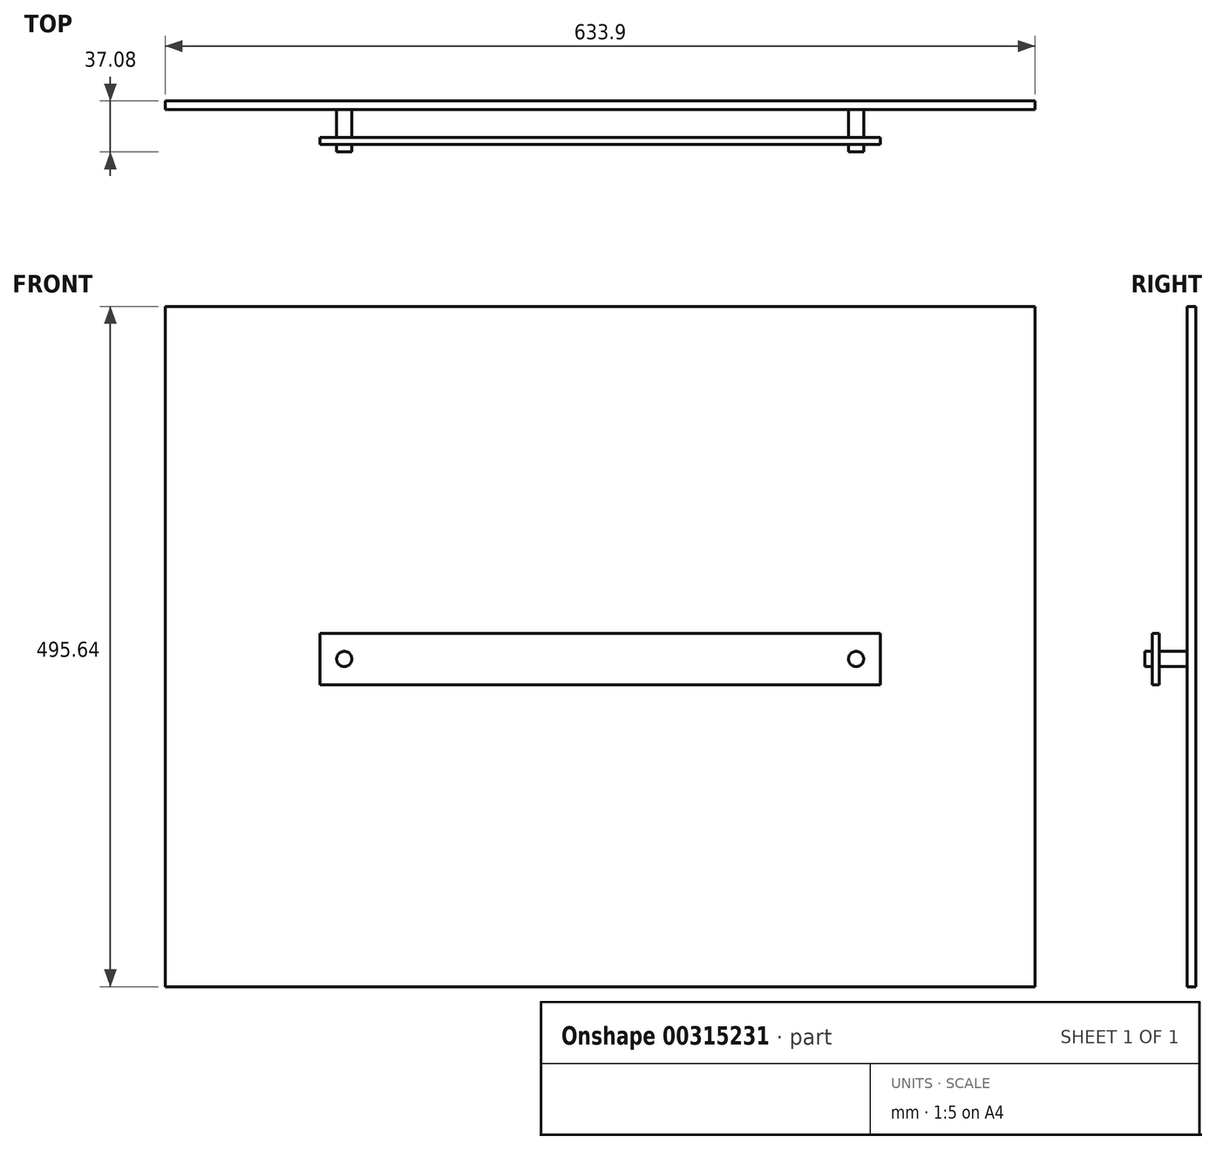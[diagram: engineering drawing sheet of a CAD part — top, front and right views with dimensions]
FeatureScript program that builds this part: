
annotation { "Feature Type Name" : "Feature", "Feature Type Description" : "" }
export const myFeature = defineFeature(function(context is Context, id is Id, definition is map)
    precondition{}
    {
        {
            var Q0;
            Q0=qCreatedBy(makeId("Front.planeOp"),FACE);
            var sketch = newSketch(context, id + "F0", { "sketchPlane" : qUnion([Q0])});
            skLineSegment(sketch, "E0.bottom", {"start": v(204.28, 9.68) * mm, "end": v(-204.28, 9.68) * mm});
            skLineSegment(sketch, "E0.top", {"start": v(204.28, -27.91) * mm, "end": v(-204.28, -27.91) * mm});
            skLineSegment(sketch, "E0.left", {"start": v(204.28, 9.68) * mm, "end": v(204.28, -27.91) * mm});
            skLineSegment(sketch, "E0.right", {"start": v(-204.28, 9.68) * mm, "end": v(-204.28, -27.91) * mm});
            skPoint(sketch, "E0.middle", {"position": v(0, -9.12) * mm});
            skSolve(sketch);
        }
        {
            var Q0;
            Q0 = qSketchRegion(id + "F0", true);
            extrude(context, id + "F1", {"entities" : qUnion([Q0]), "depth" : 5.08 * mm});
        }
        {
            var Q0;
            Q0=makeQuery(id+"F1.opExtrude","CAP_FACE",FACE,{"disambiguationData":[OSD([sQuery(id+"F0.wireOp",EDGE,"E0.bottom"),sQuery(id+"F0.wireOp",EDGE,"E0.top"),sQuery(id+"F0.wireOp",EDGE,"E0.left"),sQuery(id+"F0.wireOp",EDGE,"E0.right")])],"isStart":false});
            var sketch = newSketch(context, id + "F2", { "sketchPlane" : qUnion([Q0])});
            skLineSegment(sketch, "E1", {"start": v(-204.28, -9.12) * mm, "end": v(204.28, -9.12) * mm});
            skCircle(sketch, "E2", {"center": v(-186.46, -9.12) * mm, "radius": 5.54 * mm});
            skSolve(sketch);
        }
        {
            var Q0;
            Q0 = qSketchRegion(id + "F2", true);
            extrude(context, id + "F3", {"entities" : qUnion([Q0]), "depth" : 5.33 * mm, "hasSecondDirection" : true, "secondDirectionOppositeDirection" : true, "secondDirectionDepth" : 25.4 * mm});
        }
        {
            var Q0;
            Q0=makeQuery(id+"F3.opExtrude","SWEPT_BODY",BODY,{"disambiguationData":[OSD([sQuery(id+"F2.wireOp",EDGE,"E2")])]});
            var Q1;
            Q1=qCreatedBy(makeId("Right.planeOp"),FACE);
            mirror(context, id + "F4", {"operationType" : NewBodyOperationType.ADD, "entities" : qUnion([Q0]), "mirrorPlane" : qUnion([Q1])});
        }
        {
            var Q0;
            Q0=makeQuery(id+"F3.opExtrude","CAP_FACE",FACE,{"disambiguationData":[OSD([sQuery(id+"F2.wireOp",EDGE,"E2")])],"isStart":true});
            var sketch = newSketch(context, id + "F5", { "sketchPlane" : qUnion([Q0])});
            skLineSegment(sketch, "E3.bottom", {"start": v(316.95, 247.82) * mm, "end": v(-316.95, 247.82) * mm});
            skLineSegment(sketch, "E3.top", {"start": v(316.95, -247.82) * mm, "end": v(-316.95, -247.82) * mm});
            skLineSegment(sketch, "E3.left", {"start": v(316.95, 247.82) * mm, "end": v(316.95, -247.82) * mm});
            skLineSegment(sketch, "E3.right", {"start": v(-316.95, 247.82) * mm, "end": v(-316.95, -247.82) * mm});
            skPoint(sketch, "E3.middle", {"position": v(0, 0) * mm});
            skSolve(sketch);
        }
        {
            var Q0;
            Q0 = qSketchRegion(id + "F5", true);
            extrude(context, id + "F6", {"entities" : qUnion([Q0]), "depth" : 6.35 * mm});
        }
    });
